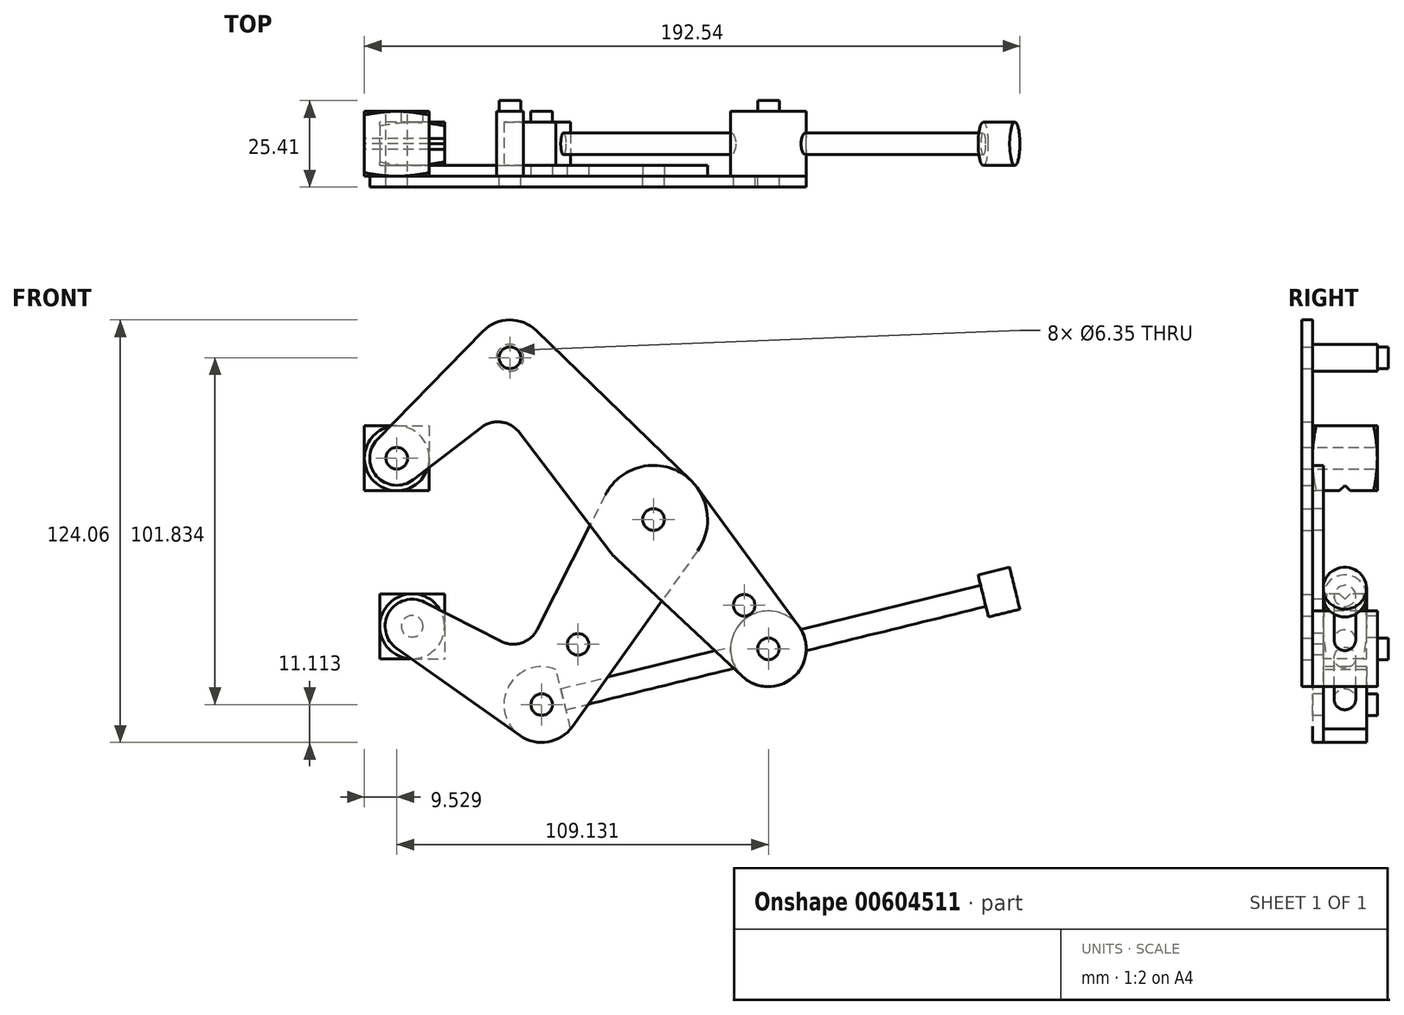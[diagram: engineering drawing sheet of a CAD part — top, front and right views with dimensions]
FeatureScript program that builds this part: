
annotation { "Feature Type Name" : "Feature", "Feature Type Description" : "" }
export const myFeature = defineFeature(function(context is Context, id is Id, definition is map)
    precondition{}
    {
        {
            var Q0;
            Q0=qCreatedBy(makeId("Front.planeOp"),FACE);
            var sketch = newSketch(context, id + "F0", { "sketchPlane" : qUnion([Q0])});
            skCircle(sketch, "E0", {"center": v(-64.57, 13.24) * mm, "radius": 7.94 * mm});
            skLineSegment(sketch, "E1", {"start": v(-64.57, 13.24) * mm, "end": v(-31.33, 42.76) * mm, "construction": true});
            skLineSegment(sketch, "E2", {"start": v(-31.33, 42.76) * mm, "end": v(10.83, -4.72) * mm, "construction": true});
            skLineSegment(sketch, "E3", {"start": v(10.83, -4.72) * mm, "end": v(44.56, -42.7) * mm, "construction": true});
            skCircle(sketch, "E4", {"center": v(10.83, -4.72) * mm, "radius": 15.88 * mm});
            skCircle(sketch, "E5", {"center": v(44.56, -42.7) * mm, "radius": 11.11 * mm});
            skCircle(sketch, "E6", {"center": v(-31.33, 42.76) * mm, "radius": 11.11 * mm});
            skCircle(sketch, "E7", {"center": v(10.83, -4.72) * mm, "radius": 3.98 * mm});
            skLineSegment(sketch, "E8", {"start": v(10.83, -4.72) * mm, "end": v(-22, -59.08) * mm, "construction": true});
            skLineSegment(sketch, "E9", {"start": v(-22, -59.08) * mm, "end": v(-60.05, -36.1) * mm, "construction": true});
            skCircle(sketch, "E10", {"center": v(-60.05, -36.1) * mm, "radius": 7.94 * mm});
            skCircle(sketch, "E11", {"center": v(-22, -59.08) * mm, "radius": 11.11 * mm});
            skLineSegment(sketch, "E12", {"start": v(-22, -59.08) * mm, "end": v(-11.33, -41.4) * mm, "construction": true});
            skCircle(sketch, "E13", {"center": v(-11.33, -41.4) * mm, "radius": 3.18 * mm});
            skLineSegment(sketch, "E14", {"start": v(10.83, -4.72) * mm, "end": v(35.08, -32.04) * mm, "construction": true});
            skLineSegment(sketch, "E15", {"start": v(35.08, -32.04) * mm, "end": v(37.46, -29.93) * mm, "construction": true});
            skCircle(sketch, "E16", {"center": v(37.46, -29.93) * mm, "radius": 3.17 * mm});
            skCircle(sketch, "E17", {"center": v(44.56, -42.7) * mm, "radius": 3.18 * mm});
            skCircle(sketch, "E18", {"center": v(-31.33, 42.76) * mm, "radius": 3.18 * mm});
            skCircle(sketch, "E19", {"center": v(10.83, -4.72) * mm, "radius": 3.18 * mm});
            skCircle(sketch, "E20", {"center": v(-64.57, 13.24) * mm, "radius": 3.18 * mm});
            skCircle(sketch, "E21", {"center": v(-60.05, -36.1) * mm, "radius": 3.18 * mm});
            skCircle(sketch, "E22", {"center": v(-22, -59.08) * mm, "radius": 3.18 * mm});
            skLineSegment(sketch, "E23", {"start": v(-70.25, 18.79) * mm, "end": v(-39.29, 50.52) * mm});
            skLineSegment(sketch, "E24", {"start": v(-59.74, 6.95) * mm, "end": v(-39.74, 22.3) * mm});
            skLineSegment(sketch, "E25", {"start": v(-23.6, 50.74) * mm, "end": v(21.88, 6.68) * mm});
            skLineSegment(sketch, "E26", {"start": v(-28.58, 20.8) * mm, "end": v(-1.8, -14.35) * mm});
            skPoint(sketch, "E27", {"position": v(-33.41, 27.15) * mm});
            skLineSegment(sketch, "E28", {"start": v(23.64, 4.66) * mm, "end": v(53.52, -36.14) * mm});
            skLineSegment(sketch, "E29", {"start": v(0, -16.33) * mm, "end": v(36.98, -50.83) * mm});
            skLineSegment(sketch, "E30", {"start": v(23.76, -13.93) * mm, "end": v(-12.95, -65.52) * mm});
            skLineSegment(sketch, "E31", {"start": v(-64.63, -42.58) * mm, "end": v(-28.42, -68.15) * mm});
            skLineSegment(sketch, "E32", {"start": v(-56.44, -29.02) * mm, "end": v(-34, -40.48) * mm});
            skLineSegment(sketch, "E33", {"start": v(-3.34, 2.44) * mm, "end": v(-23.28, -36.99) * mm});
            skPoint(sketch, "E34", {"position": v(-26.89, -44.1) * mm});
            skArc(sketch, "E35.filletArc", {"start": v(-28.58, 20.8) * mm, "mid": v(-33.85, 23.87) * mm, "end": v(-39.74, 22.3) * mm});
            skArc(sketch, "E36.filletArc", {"start": v(-34, -40.48) * mm, "mid": v(-27.91, -40.96) * mm, "end": v(-23.28, -36.99) * mm});
            skSolve(sketch);
        }
        {
            var Q0;
            Q0=makeQuery(id+"F0.imprint","IMPRINT",FACE,{"disambiguationData":[TD([[makeQuery(id+"F0.imprint","IMPRINT",EDGE,{"derivedFrom":sQuery(id+"F0.wireOp",EDGE,"E13")}),-1.0]])]});
            var Q1;
            {var subQ0=sQuery(id+"F0.wireOp",EDGE,"E26");var subQ1=sQuery(id+"F0.wireOp",EDGE,"E4");var subQ2=makeQuery(id+"F0.imprint","INTERSECT",VERTEX,{"derivedFrom":[subQ1,subQ0]});Q1=makeQuery(id+"F0.imprint","IMPRINT",FACE,{"disambiguationData":[TD([[makeQuery(id+"F0.imprint","IMPRINT",EDGE,{"disambiguationData":[TD([[subQ2,1.0]])],"derivedFrom":subQ1}),-1.0]])]});}
            var Q2;
            Q2=makeQuery(id+"F0.imprint","IMPRINT",FACE,{"disambiguationData":[TD([[makeQuery(id+"F0.imprint","IMPRINT",EDGE,{"derivedFrom":sQuery(id+"F0.wireOp",EDGE,"E7")}),-1.0]])]});
            var Q3;
            {var subQ0=sQuery(id+"F0.wireOp",EDGE,"E29");var subQ1=sQuery(id+"F0.wireOp",EDGE,"E4");var subQ2=makeQuery(id+"F0.imprint","INTERSECT",VERTEX,{"derivedFrom":[subQ1,subQ0]});Q3=makeQuery(id+"F0.imprint","IMPRINT",FACE,{"disambiguationData":[TD([[makeQuery(id+"F0.imprint","IMPRINT",EDGE,{"disambiguationData":[TD([[subQ2,-1.0]])],"derivedFrom":subQ1}),-1.0]])]});}
            var Q4;
            Q4=makeQuery(id+"F0.imprint","IMPRINT",FACE,{"disambiguationData":[TD([[makeQuery(id+"F0.imprint","IMPRINT",EDGE,{"derivedFrom":sQuery(id+"F0.wireOp",EDGE,"E21")}),-1.0]])]});
            var Q5;
            Q5=makeQuery(id+"F0.imprint","IMPRINT",FACE,{"disambiguationData":[TD([[makeQuery(id+"F0.imprint","IMPRINT",EDGE,{"derivedFrom":sQuery(id+"F0.wireOp",EDGE,"E22")}),-1.0]])]});
            var Q6;
            Q6=makeQuery(id+"F0.imprint","IMPRINT",FACE,{"disambiguationData":[TD([[makeQuery(id+"F0.imprint","IMPRINT",EDGE,{"derivedFrom":sQuery(id+"F0.wireOp",EDGE,"E7")}),1.0]])]});
            extrude(context, id + "F1", {"entities" : qUnion([Q0, Q1, Q2, Q3, Q4, Q5, Q6]), "oppositeDirection" : true, "depth" : 3.17 * mm, "offsetDistance" : 25.4 * mm});
        }
        {
            var Q0;
            {var subQ0=sQuery(id+"F0.wireOp",EDGE,"E23");Q0=makeQuery(id+"F0.imprint","IMPRINT",FACE,{"disambiguationData":[TD([[makeQuery(id+"F0.imprint","IMPRINT",EDGE,{"derivedFrom":subQ0}),-1.0]])]});}
            var Q1;
            Q1=makeQuery(id+"F0.imprint","IMPRINT",FACE,{"disambiguationData":[TD([[makeQuery(id+"F0.imprint","IMPRINT",EDGE,{"derivedFrom":sQuery(id+"F0.wireOp",EDGE,"E20")}),-1.0]])]});
            var Q2;
            Q2=makeQuery(id+"F0.imprint","IMPRINT",FACE,{"disambiguationData":[TD([[makeQuery(id+"F0.imprint","IMPRINT",EDGE,{"derivedFrom":sQuery(id+"F0.wireOp",EDGE,"E18")}),-1.0]])]});
            var Q3;
            Q3=makeQuery(id+"F0.imprint","IMPRINT",FACE,{"disambiguationData":[TD([[makeQuery(id+"F0.imprint","IMPRINT",EDGE,{"derivedFrom":sQuery(id+"F0.wireOp",EDGE,"E7")}),-1.0]])]});
            var Q4;
            {var subQ0=sQuery(id+"F0.wireOp",EDGE,"E26");var subQ1=sQuery(id+"F0.wireOp",EDGE,"E4");var subQ2=makeQuery(id+"F0.imprint","INTERSECT",VERTEX,{"derivedFrom":[subQ1,subQ0]});Q4=makeQuery(id+"F0.imprint","IMPRINT",FACE,{"disambiguationData":[TD([[makeQuery(id+"F0.imprint","IMPRINT",EDGE,{"disambiguationData":[TD([[subQ2,1.0]])],"derivedFrom":subQ1}),-1.0]])]});}
            var Q5;
            {var subQ0=sQuery(id+"F0.wireOp",EDGE,"E29");var subQ1=sQuery(id+"F0.wireOp",EDGE,"E4");var subQ2=makeQuery(id+"F0.imprint","INTERSECT",VERTEX,{"derivedFrom":[subQ1,subQ0]});Q5=makeQuery(id+"F0.imprint","IMPRINT",FACE,{"disambiguationData":[TD([[makeQuery(id+"F0.imprint","IMPRINT",EDGE,{"disambiguationData":[TD([[subQ2,-1.0]])],"derivedFrom":subQ1}),-1.0]])]});}
            var Q6;
            Q6=makeQuery(id+"F0.imprint","IMPRINT",FACE,{"disambiguationData":[TD([[makeQuery(id+"F0.imprint","IMPRINT",EDGE,{"derivedFrom":sQuery(id+"F0.wireOp",EDGE,"E7")}),1.0]])]});
            var Q7;
            Q7=makeQuery(id+"F0.imprint","IMPRINT",FACE,{"disambiguationData":[TD([[makeQuery(id+"F0.imprint","IMPRINT",EDGE,{"derivedFrom":sQuery(id+"F0.wireOp",EDGE,"E16")}),-1.0]])]});
            var Q8;
            Q8=makeQuery(id+"F0.imprint","IMPRINT",FACE,{"disambiguationData":[TD([[makeQuery(id+"F0.imprint","IMPRINT",EDGE,{"derivedFrom":sQuery(id+"F0.wireOp",EDGE,"E17")}),-1.0]])]});
            extrude(context, id + "F2", {"entities" : qUnion([Q0, Q1, Q2, Q3, Q4, Q5, Q6, Q7, Q8]), "depth" : 3.17 * mm, "offsetDistance" : 25.4 * mm});
        }
        {
            var Q0;
            Q0=makeQuery(id+"F2.opExtrude","CAP_FACE",FACE,{"disambiguationData":[OSD([sQuery(id+"F0.wireOp",EDGE,"E0"),sQuery(id+"F0.wireOp",EDGE,"E4"),sQuery(id+"F0.wireOp",EDGE,"E5"),sQuery(id+"F0.wireOp",EDGE,"E6"),sQuery(id+"F0.wireOp",EDGE,"E16"),sQuery(id+"F0.wireOp",EDGE,"E17"),sQuery(id+"F0.wireOp",EDGE,"E18"),sQuery(id+"F0.wireOp",EDGE,"E19"),sQuery(id+"F0.wireOp",EDGE,"E20"),sQuery(id+"F0.wireOp",EDGE,"E23"),sQuery(id+"F0.wireOp",EDGE,"E24"),sQuery(id+"F0.wireOp",EDGE,"E25"),sQuery(id+"F0.wireOp",EDGE,"E26"),sQuery(id+"F0.wireOp",EDGE,"E28"),sQuery(id+"F0.wireOp",EDGE,"E29"),sQuery(id+"F0.wireOp",EDGE,"E35.filletArc")])],"isStart":false});
            var sketch = newSketch(context, id + "F3", { "sketchPlane" : qUnion([Q0])});
            skCircle(sketch, "E37", {"center": v(-31.33, 42.76) * mm, "radius": 3.98 * mm});
            skCircle(sketch, "E38", {"center": v(10.83, -4.72) * mm, "radius": 3.98 * mm});
            skCircle(sketch, "E39", {"center": v(44.56, -42.7) * mm, "radius": 11.11 * mm});
            skSolve(sketch);
        }
        {
            var Q0;
            Q0=qCreatedBy(makeId("Front.planeOp"),FACE);
            var sketch = newSketch(context, id + "F4", { "sketchPlane" : qUnion([Q0])});
            skCircle(sketch, "E40", {"center": v(-60.05, -36.1) * mm, "radius": 3.98 * mm});
            skCircle(sketch, "E41", {"center": v(-22, -59.08) * mm, "radius": 11.11 * mm});
            skLineSegment(sketch, "E42", {"start": v(-15.65, -57.52) * mm, "end": v(44.56, -42.7) * mm, "construction": true});
            skLineSegment(sketch, "E43", {"start": v(-22, -59.08) * mm, "end": v(-15.65, -57.52) * mm, "construction": true});
            skLineSegment(sketch, "E44", {"start": v(-15.65, -57.52) * mm, "end": v(-17.8, -48.8) * mm});
            skLineSegment(sketch, "E45", {"start": v(-15.65, -57.52) * mm, "end": v(-13.5, -66.24) * mm});
            skPoint(sketch, "E46", {"position": v(44.56, -42.7) * mm});
            skSolve(sketch);
        }
        {
            var Q0;
            Q0=qCreatedBy(makeId("Front.planeOp"),FACE);
            cPlane(context, id + "F5", {"entities" : qUnion([Q0]), "cplaneType" : CPlaneType.OFFSET, "offset" : 9.52 * mm, "oppositeDirection" : true, "width" : 152.4 * mm, "height" : 152.4 * mm});
        }
        {
            var Q0;
            Q0=makeQuery(id+"F3.imprint","IMPRINT",FACE,{"disambiguationData":[TD([[makeQuery(id+"F3.imprint","IMPRINT",EDGE,{"derivedFrom":makeQuery(id+"F2.opExtrude","CAP_EDGE",EDGE,{"disambiguationData":[OSD([sQuery(id+"F0.wireOp",EDGE,"E17")])],"isStart":false})}),-1.0]])]});
            var Q1;
            Q1=makeQuery(id+"F3.imprint","IMPRINT",FACE,{"disambiguationData":[TD([[makeQuery(id+"F3.imprint","IMPRINT",EDGE,{"derivedFrom":sQuery(id+"F3.wireOp",EDGE,"E37")}),1.0]])]});
            var Q2;
            Q2=makeQuery(id+"F3.imprint","IMPRINT",FACE,{"disambiguationData":[TD([[makeQuery(id+"F3.imprint","IMPRINT",EDGE,{"derivedFrom":makeQuery(id+"F2.opExtrude","CAP_EDGE",EDGE,{"disambiguationData":[OSD([sQuery(id+"F0.wireOp",EDGE,"E18")])],"isStart":false})}),1.0]])]});
            var Q3;
            Q3=makeQuery(id+"F3.imprint","IMPRINT",FACE,{"disambiguationData":[TD([[makeQuery(id+"F3.imprint","IMPRINT",EDGE,{"derivedFrom":makeQuery(id+"F2.opExtrude","CAP_EDGE",EDGE,{"disambiguationData":[OSD([sQuery(id+"F0.wireOp",EDGE,"E17")])],"isStart":false})}),1.0]])]});
            var Q4;
            Q4=makeQuery(id+"F4.imprint","IMPRINT",FACE,{"disambiguationData":[TD([[makeQuery(id+"F4.imprint","IMPRINT",EDGE,{"derivedFrom":makeQuery(id+"F1.opExtrude","CAP_EDGE",EDGE,{"disambiguationData":[OSD([sQuery(id+"F0.wireOp",EDGE,"E21")])],"isStart":true})}),1.0]])]});
            var Q5;
            Q5=makeQuery(id+"F4.imprint","IMPRINT",FACE,{"disambiguationData":[TD([[makeQuery(id+"F4.imprint","IMPRINT",EDGE,{"derivedFrom":sQuery(id+"F4.wireOp",EDGE,"E40")}),1.0]])]});
            var Q6;
            {var subQ0=sQuery(id+"F4.wireOp",EDGE,"E44");Q6=makeQuery(id+"F4.imprint","IMPRINT",FACE,{"disambiguationData":[TD([[makeQuery(id+"F4.imprint","IMPRINT",EDGE,{"derivedFrom":subQ0}),1.0]])]});}
            var Q7;
            Q7=makeQuery(id+"F4.imprint","IMPRINT",FACE,{"disambiguationData":[TD([[makeQuery(id+"F4.imprint","IMPRINT",EDGE,{"derivedFrom":makeQuery(id+"F1.opExtrude","CAP_EDGE",EDGE,{"disambiguationData":[OSD([sQuery(id+"F0.wireOp",EDGE,"E22")])],"isStart":true})}),1.0]])]});
            var Q8;
            Q8=qCreatedBy(id+"F5.planeOp",FACE);
            extrude(context, id + "F6", {"entities" : qUnion([Q0, Q1, Q2, Q3, Q4, Q5, Q6, Q7]), "endBound" : BoundingType.UP_TO_SURFACE, "oppositeDirection" : true, "depth" : 25.4 * mm, "endBoundEntityFace" : qUnion([Q8]), "offsetDistance" : 25.4 * mm});
        }
        {
            var Q0;
            Q0=makeQuery(id+"F2.opExtrude","SWEPT_BODY",BODY,{"disambiguationData":[OSD([sQuery(id+"F0.wireOp",EDGE,"E0"),sQuery(id+"F0.wireOp",EDGE,"E4"),sQuery(id+"F0.wireOp",EDGE,"E5"),sQuery(id+"F0.wireOp",EDGE,"E6"),sQuery(id+"F0.wireOp",EDGE,"E16"),sQuery(id+"F0.wireOp",EDGE,"E17"),sQuery(id+"F0.wireOp",EDGE,"E18"),sQuery(id+"F0.wireOp",EDGE,"E19"),sQuery(id+"F0.wireOp",EDGE,"E20"),sQuery(id+"F0.wireOp",EDGE,"E23"),sQuery(id+"F0.wireOp",EDGE,"E24"),sQuery(id+"F0.wireOp",EDGE,"E25"),sQuery(id+"F0.wireOp",EDGE,"E26"),sQuery(id+"F0.wireOp",EDGE,"E28"),sQuery(id+"F0.wireOp",EDGE,"E29"),sQuery(id+"F0.wireOp",EDGE,"E35.filletArc")])]});
            var Q1;
            Q1=makeQuery(id+"F6.opExtrude","SWEPT_BODY",BODY,{"disambiguationData":[OSD([sQuery(id+"F3.wireOp",EDGE,"E39")])]});
            var Q2;
            Q2=makeQuery(id+"F6.opExtrude","SWEPT_BODY",BODY,{"disambiguationData":[OSD([sQuery(id+"F3.wireOp",EDGE,"E37")])]});
            booleanBodies(context, id + "F7", {"operationType" : BooleanOperationType.SUBTRACTION, "tools" : qUnion([Q0]), "targets" : qUnion([Q1, Q2]), "keepTools" : true});
        }
        {
            var Q0;
            Q0=makeQuery(id+"F1.opExtrude","SWEPT_BODY",BODY,{"disambiguationData":[OSD([sQuery(id+"F0.wireOp",EDGE,"E4"),sQuery(id+"F0.wireOp",EDGE,"E10"),sQuery(id+"F0.wireOp",EDGE,"E11"),sQuery(id+"F0.wireOp",EDGE,"E13"),sQuery(id+"F0.wireOp",EDGE,"E19"),sQuery(id+"F0.wireOp",EDGE,"E21"),sQuery(id+"F0.wireOp",EDGE,"E22"),sQuery(id+"F0.wireOp",EDGE,"E30"),sQuery(id+"F0.wireOp",EDGE,"E31"),sQuery(id+"F0.wireOp",EDGE,"E32"),sQuery(id+"F0.wireOp",EDGE,"E33"),sQuery(id+"F0.wireOp",EDGE,"E36.filletArc")])]});
            var Q1;
            Q1=makeQuery(id+"F6.opExtrude","SWEPT_BODY",BODY,{"disambiguationData":[OSD([sQuery(id+"F4.wireOp",EDGE,"E41"),sQuery(id+"F4.wireOp",EDGE,"E44"),sQuery(id+"F4.wireOp",EDGE,"E45")])]});
            var Q2;
            Q2=makeQuery(id+"F6.opExtrude","SWEPT_BODY",BODY,{"disambiguationData":[OSD([sQuery(id+"F4.wireOp",EDGE,"E40")])]});
            booleanBodies(context, id + "F8", {"operationType" : BooleanOperationType.SUBTRACTION, "tools" : qUnion([Q0]), "targets" : qUnion([Q1, Q2]), "keepTools" : true});
        }
        {
            var Q0;
            Q0=makeQuery(id+"F6.opExtrude","SWEPT_BODY",BODY,{"disambiguationData":[OSD([sQuery(id+"F3.wireOp",EDGE,"E37")])]});
            var Q1;
            Q1=makeQuery(id+"F6.opExtrude","SWEPT_BODY",BODY,{"disambiguationData":[OSD([sQuery(id+"F3.wireOp",EDGE,"E39")])]});
            var Q2;
            Q2=makeQuery(id+"F6.opExtrude","SWEPT_BODY",BODY,{"disambiguationData":[OSD([sQuery(id+"F4.wireOp",EDGE,"E41"),sQuery(id+"F4.wireOp",EDGE,"E44"),sQuery(id+"F4.wireOp",EDGE,"E45")])]});
            var Q3;
            Q3=makeQuery(id+"F6.opExtrude","SWEPT_BODY",BODY,{"disambiguationData":[OSD([sQuery(id+"F4.wireOp",EDGE,"E40")])]});
            var Q4;
            Q4=qCreatedBy(id+"F5.planeOp",FACE);
            mirror(context, id + "F9", {"entities" : qUnion([Q0, Q1, Q2, Q3]), "mirrorPlane" : qUnion([Q4])});
        }
        {
            var Q0;
            Q0=makeQuery(id+"F6.opExtrude","SWEPT_BODY",BODY,{"disambiguationData":[OSD([sQuery(id+"F3.wireOp",EDGE,"E37")])]});
            var Q1;
            Q1=makeQuery(id+"F9.opPattern","COPY",BODY,{"derivedFrom":makeQuery(id+"F6.opExtrude","SWEPT_BODY",BODY,{"disambiguationData":[OSD([sQuery(id+"F3.wireOp",EDGE,"E37")])]}),"instanceName":"1"});
            var Q2;
            Q2=makeQuery(id+"F6.opExtrude","SWEPT_BODY",BODY,{"disambiguationData":[OSD([sQuery(id+"F3.wireOp",EDGE,"E39")])]});
            var Q3;
            Q3=makeQuery(id+"F6.opExtrude","SWEPT_BODY",BODY,{"disambiguationData":[OSD([sQuery(id+"F4.wireOp",EDGE,"E40")])]});
            var Q4;
            Q4=makeQuery(id+"F6.opExtrude","SWEPT_BODY",BODY,{"disambiguationData":[OSD([sQuery(id+"F4.wireOp",EDGE,"E41"),sQuery(id+"F4.wireOp",EDGE,"E44"),sQuery(id+"F4.wireOp",EDGE,"E45")])]});
            var Q5;
            Q5=makeQuery(id+"F9.opPattern","COPY",BODY,{"derivedFrom":makeQuery(id+"F6.opExtrude","SWEPT_BODY",BODY,{"disambiguationData":[OSD([sQuery(id+"F3.wireOp",EDGE,"E39")])]}),"instanceName":"1"});
            var Q6;
            Q6=makeQuery(id+"F9.opPattern","COPY",BODY,{"derivedFrom":makeQuery(id+"F6.opExtrude","SWEPT_BODY",BODY,{"disambiguationData":[OSD([sQuery(id+"F4.wireOp",EDGE,"E40")])]}),"instanceName":"1"});
            var Q7;
            Q7=makeQuery(id+"F9.opPattern","COPY",BODY,{"derivedFrom":makeQuery(id+"F6.opExtrude","SWEPT_BODY",BODY,{"disambiguationData":[OSD([sQuery(id+"F4.wireOp",EDGE,"E41"),sQuery(id+"F4.wireOp",EDGE,"E44"),sQuery(id+"F4.wireOp",EDGE,"E45")])]}),"instanceName":"1"});
            booleanBodies(context, id + "F10", {"operationType" : BooleanOperationType.UNION, "tools" : qUnion([Q0, Q1, Q2, Q3, Q4, Q5, Q6, Q7])});
        }
        {
            var Q0;
            {var subQ0=makeQuery(id+"F6.opExtrude","SWEPT_FACE",FACE,{"disambiguationData":[OSD([sQuery(id+"F4.wireOp",EDGE,"E44"),sQuery(id+"F4.wireOp",EDGE,"E45")])]});Q0=makeQuery(id+"F10.opBoolean","MERGE",FACE,{"derivedFrom":[subQ0,makeQuery(id+"F9.opPattern","COPY",FACE,{"derivedFrom":subQ0,"instanceName":"1"})]});}
            var sketch = newSketch(context, id + "F11", { "sketchPlane" : qUnion([Q0])});
            skLineSegment(sketch, "E47", {"start": v(9.53, -61.1) * mm, "end": v(9.53, -43.13) * mm, "construction": true});
            skLineSegment(sketch, "E48", {"start": v(3.18, -52.11) * mm, "end": v(15.88, -52.11) * mm, "construction": true});
            skCircle(sketch, "E49", {"center": v(9.53, -52.11) * mm, "radius": 3.18 * mm});
            skSolve(sketch);
        }
        {
            var Q0;
            Q0=makeQuery(id+"F11.imprint","IMPRINT",FACE,{"disambiguationData":[TD([[makeQuery(id+"F11.imprint","IMPRINT",EDGE,{"derivedFrom":sQuery(id+"F11.wireOp",EDGE,"E49")}),1.0]])]});
            extrude(context, id + "F12", {"entities" : qUnion([Q0]), "oppositeDirection" : true, "depth" : 12.7 * mm, "offsetDistance" : 25.4 * mm});
        }
        {
            var Q0;
            Q0=makeQuery(id+"F12.opExtrude","CAP_FACE",FACE,{"disambiguationData":[OSD([sQuery(id+"F11.wireOp",EDGE,"E49")])],"isStart":true});
            extrude(context, id + "F13", {"entities" : qUnion([Q0]), "operationType" : NewBodyOperationType.ADD, "depth" : 127 * mm, "offsetDistance" : 25.4 * mm});
        }
        {
            var Q0;
            Q0=makeQuery(id+"F13.opExtrude","CAP_FACE",FACE,{"disambiguationData":[OSD([sQuery(id+"F11.wireOp",EDGE,"E49")])],"isStart":false});
            var sketch = newSketch(context, id + "F14", { "sketchPlane" : qUnion([Q0])});
            skCircle(sketch, "E50", {"center": v(9.53, -52.11) * mm, "radius": 6.35 * mm});
            skSolve(sketch);
        }
        {
            var Q0;
            Q0=makeQuery(id+"F14.imprint","IMPRINT",FACE,{"disambiguationData":[TD([[makeQuery(id+"F14.imprint","IMPRINT",EDGE,{"derivedFrom":sQuery(id+"F14.wireOp",EDGE,"E50")}),1.0]])]});
            var Q1;
            Q1=makeQuery(id+"F14.imprint","IMPRINT",FACE,{"disambiguationData":[TD([[makeQuery(id+"F14.imprint","IMPRINT",EDGE,{"derivedFrom":makeQuery(id+"F13.opExtrude","CAP_EDGE",EDGE,{"disambiguationData":[OSD([sQuery(id+"F11.wireOp",EDGE,"E49")])],"isStart":false})}),1.0]])]});
            extrude(context, id + "F15", {"entities" : qUnion([Q0, Q1]), "operationType" : NewBodyOperationType.ADD, "depth" : 9.52 * mm, "offsetDistance" : 25.4 * mm});
        }
        {
            var Q0;
            Q0=makeQuery(id+"F1.opExtrude","CAP_FACE",FACE,{"disambiguationData":[OSD([sQuery(id+"F0.wireOp",EDGE,"E4"),sQuery(id+"F0.wireOp",EDGE,"E10"),sQuery(id+"F0.wireOp",EDGE,"E11"),sQuery(id+"F0.wireOp",EDGE,"E13"),sQuery(id+"F0.wireOp",EDGE,"E19"),sQuery(id+"F0.wireOp",EDGE,"E21"),sQuery(id+"F0.wireOp",EDGE,"E22"),sQuery(id+"F0.wireOp",EDGE,"E30"),sQuery(id+"F0.wireOp",EDGE,"E31"),sQuery(id+"F0.wireOp",EDGE,"E32"),sQuery(id+"F0.wireOp",EDGE,"E33"),sQuery(id+"F0.wireOp",EDGE,"E36.filletArc")])],"isStart":false});
            var sketch = newSketch(context, id + "F16", { "sketchPlane" : qUnion([Q0])});
            skLineSegment(sketch, "E51.bottom", {"start": v(69.58, -26.57) * mm, "end": v(50.53, -26.57) * mm});
            skLineSegment(sketch, "E51.top", {"start": v(69.58, -45.62) * mm, "end": v(50.53, -45.62) * mm});
            skLineSegment(sketch, "E51.left", {"start": v(69.58, -26.57) * mm, "end": v(69.58, -45.62) * mm});
            skLineSegment(sketch, "E51.right", {"start": v(50.53, -26.57) * mm, "end": v(50.53, -45.62) * mm});
            skPoint(sketch, "E51.middle", {"position": v(60.05, -36.1) * mm});
            skPoint(sketch, "E52.middle", {"position": v(64.57, 13.24) * mm});
            skSolve(sketch);
        }
        {
            var Q0;
            {var subQ1=sQuery(id+"F16.wireOp",EDGE,"E51.bottom");Q0=makeQuery(id+"F16.imprint","IMPRINT",FACE,{"disambiguationData":[TD([[makeQuery(id+"F16.imprint","IMPRINT",EDGE,{"derivedFrom":subQ1}),1.0]])]});}
            var Q1;
            {var subQ5=makeQuery(id+"F1.opExtrude","CAP_EDGE",EDGE,{"disambiguationData":[OSD([sQuery(id+"F0.wireOp",EDGE,"E10")])],"isStart":false});Q1=makeQuery(id+"F16.imprint","IMPRINT",FACE,{"disambiguationData":[TD([[makeQuery(id+"F16.imprint","IMPRINT",EDGE,{"derivedFrom":subQ5}),-1.0]])]});}
            var Q2;
            Q2=qCreatedBy(id+"F5.planeOp",FACE);
            extrude(context, id + "F17", {"entities" : qUnion([Q0, Q1]), "endBound" : BoundingType.UP_TO_SURFACE, "depth" : 25.4 * mm, "endBoundEntityFace" : qUnion([Q2]), "offsetDistance" : 25.4 * mm});
        }
        {
            var Q0;
            Q0=makeQuery(id+"F2.opExtrude","CAP_FACE",FACE,{"disambiguationData":[OSD([sQuery(id+"F0.wireOp",EDGE,"E0"),sQuery(id+"F0.wireOp",EDGE,"E4"),sQuery(id+"F0.wireOp",EDGE,"E5"),sQuery(id+"F0.wireOp",EDGE,"E6"),sQuery(id+"F0.wireOp",EDGE,"E16"),sQuery(id+"F0.wireOp",EDGE,"E17"),sQuery(id+"F0.wireOp",EDGE,"E18"),sQuery(id+"F0.wireOp",EDGE,"E19"),sQuery(id+"F0.wireOp",EDGE,"E20"),sQuery(id+"F0.wireOp",EDGE,"E23"),sQuery(id+"F0.wireOp",EDGE,"E24"),sQuery(id+"F0.wireOp",EDGE,"E25"),sQuery(id+"F0.wireOp",EDGE,"E26"),sQuery(id+"F0.wireOp",EDGE,"E28"),sQuery(id+"F0.wireOp",EDGE,"E29"),sQuery(id+"F0.wireOp",EDGE,"E35.filletArc")])],"isStart":true});
            var sketch = newSketch(context, id + "F18", { "sketchPlane" : qUnion([Q0])});
            skLineSegment(sketch, "E53.bottom", {"start": v(74.1, 22.77) * mm, "end": v(55.05, 22.77) * mm});
            skLineSegment(sketch, "E53.top", {"start": v(74.1, 3.72) * mm, "end": v(55.05, 3.72) * mm});
            skLineSegment(sketch, "E53.left", {"start": v(74.1, 22.77) * mm, "end": v(74.1, 3.72) * mm});
            skLineSegment(sketch, "E53.right", {"start": v(55.05, 22.77) * mm, "end": v(55.05, 3.72) * mm});
            skPoint(sketch, "E53.middle", {"position": v(64.57, 13.24) * mm});
            skSolve(sketch);
        }
        {
            var Q0;
            {var subQ1=sQuery(id+"F18.wireOp",EDGE,"E53.top");Q0=makeQuery(id+"F18.imprint","IMPRINT",FACE,{"disambiguationData":[TD([[makeQuery(id+"F18.imprint","IMPRINT",EDGE,{"derivedFrom":subQ1}),-1.0]])]});}
            var Q1;
            {var subQ5=makeQuery(id+"F2.opExtrude","CAP_EDGE",EDGE,{"disambiguationData":[OSD([sQuery(id+"F0.wireOp",EDGE,"E0")])],"isStart":true});Q1=makeQuery(id+"F18.imprint","IMPRINT",FACE,{"disambiguationData":[TD([[makeQuery(id+"F18.imprint","IMPRINT",EDGE,{"derivedFrom":subQ5}),-1.0]])]});}
            var Q2;
            Q2=qCreatedBy(id+"F5.planeOp",FACE);
            extrude(context, id + "F19", {"entities" : qUnion([Q0, Q1]), "endBound" : BoundingType.UP_TO_SURFACE, "depth" : 25.4 * mm, "endBoundEntityFace" : qUnion([Q2]), "offsetDistance" : 25.4 * mm});
        }
        {
            var Q0;
            Q0=makeQuery(id+"F19.opExtrude","SWEPT_FACE",FACE,{"disambiguationData":[OSD([sQuery(id+"F18.wireOp",EDGE,"E53.bottom")])]});
            var sketch = newSketch(context, id + "F20", { "sketchPlane" : qUnion([Q0])});
            skLineSegment(sketch, "E54", {"start": v(-64.57, 9.53) * mm, "end": v(-64.57, 0) * mm});
            skSolve(sketch);
        }
        {
            var Q0;
            Q0=makeQuery(id+"F19.opExtrude","SWEPT_FACE",FACE,{"disambiguationData":[OSD([sQuery(id+"F18.wireOp",EDGE,"E53.left")])]});
            cPlane(context, id + "F21", {"entities" : qUnion([Q0]), "cplaneType" : CPlaneType.OFFSET, "offset" : 9.52 * mm, "oppositeDirection" : true, "width" : 152.4 * mm, "height" : 152.4 * mm});
        }
        {
            var Q0;
            Q0=qCreatedBy(id+"F21.planeOp",FACE);
            var sketch = newSketch(context, id + "F22", { "sketchPlane" : qUnion([Q0])});
            skLineSegment(sketch, "E55", {"start": v(0, 22.77) * mm, "end": v(0, 32.3) * mm});
            skLineSegment(sketch, "E56", {"start": v(0, 32.3) * mm, "end": v(-2.55, 32.3) * mm});
            skLineSegment(sketch, "E57", {"start": v(-2.55, 32.3) * mm, "end": v(0, 22.77) * mm});
            skSolve(sketch);
        }
        {
            var Q0;
            Q0=makeQuery(id+"F22.imprint","IMPRINT",FACE,{"disambiguationData":[TD([[makeQuery(id+"F22.imprint","IMPRINT",EDGE,{"derivedFrom":sQuery(id+"F22.wireOp",EDGE,"E55")}),1.0]])]});
            var Q1;
            Q1=makeQuery(id+"F19.opExtrude","CAP_EDGE",EDGE,{"disambiguationData":[OSD([sQuery(id+"F0.wireOp",EDGE,"E20")])],"isStart":false});
            revolve(context, id + "F23", {"operationType" : NewBodyOperationType.REMOVE, "entities" : qUnion([Q0]), "axis" : qUnion([Q1]), "revolveType" : RevolveType.FULL, "oppositeDirection" : true});
        }
        {
            var Q0;
            Q0=makeQuery(id+"F17.opExtrude","SWEPT_FACE",FACE,{"disambiguationData":[OSD([sQuery(id+"F16.wireOp",EDGE,"E51.bottom")])]});
            var sketch = newSketch(context, id + "F24", { "sketchPlane" : qUnion([Q0])});
            skLineSegment(sketch, "E58", {"start": v(-60.05, 9.53) * mm, "end": v(-60.05, 3.18) * mm});
            skSolve(sketch);
        }
        {
            var Q0;
            Q0=makeQuery(id+"F17.opExtrude","SWEPT_FACE",FACE,{"disambiguationData":[OSD([sQuery(id+"F16.wireOp",EDGE,"E51.left")])]});
            cPlane(context, id + "F25", {"entities" : qUnion([Q0]), "cplaneType" : CPlaneType.OFFSET, "offset" : 9.52 * mm, "oppositeDirection" : true, "width" : 152.4 * mm, "height" : 152.4 * mm});
        }
        {
            var Q0;
            Q0=qCreatedBy(id+"F25.planeOp",FACE);
            var sketch = newSketch(context, id + "F26", { "sketchPlane" : qUnion([Q0])});
            skLineSegment(sketch, "E59", {"start": v(-3.18, -26.57) * mm, "end": v(-3.18, -17.04) * mm});
            skLineSegment(sketch, "E60", {"start": v(-3.18, -17.04) * mm, "end": v(-5.73, -17.04) * mm});
            skLineSegment(sketch, "E61", {"start": v(-5.73, -17.04) * mm, "end": v(-3.18, -26.57) * mm});
            skSolve(sketch);
        }
        {
            var Q0;
            Q0=makeQuery(id+"F26.imprint","IMPRINT",FACE,{"disambiguationData":[TD([[makeQuery(id+"F26.imprint","IMPRINT",EDGE,{"derivedFrom":sQuery(id+"F26.wireOp",EDGE,"E59")}),1.0]])]});
            var Q1;
            Q1=makeQuery(id+"F1.opExtrude","CAP_EDGE",EDGE,{"disambiguationData":[OSD([sQuery(id+"F0.wireOp",EDGE,"E21")])],"isStart":true});
            revolve(context, id + "F27", {"operationType" : NewBodyOperationType.REMOVE, "entities" : qUnion([Q0]), "axis" : qUnion([Q1]), "revolveType" : RevolveType.FULL, "oppositeDirection" : true});
        }
        {
            var Q0;
            Q0=makeQuery(id+"F17.opExtrude","SWEPT_BODY",BODY,{"disambiguationData":[OSD([sQuery(id+"F0.wireOp",EDGE,"E21"),sQuery(id+"F16.wireOp",EDGE,"E51.bottom"),sQuery(id+"F16.wireOp",EDGE,"E51.top"),sQuery(id+"F16.wireOp",EDGE,"E51.left"),sQuery(id+"F16.wireOp",EDGE,"E51.right")])]});
            var Q1;
            Q1=makeQuery(id+"F17.opExtrude","CAP_FACE",FACE,{"disambiguationData":[OSD([sQuery(id+"F0.wireOp",EDGE,"E21"),sQuery(id+"F16.wireOp",EDGE,"E51.bottom"),sQuery(id+"F16.wireOp",EDGE,"E51.top"),sQuery(id+"F16.wireOp",EDGE,"E51.left"),sQuery(id+"F16.wireOp",EDGE,"E51.right")])],"isStart":false});
            mirror(context, id + "F28", {"operationType" : NewBodyOperationType.ADD, "entities" : qUnion([Q0]), "mirrorPlane" : qUnion([Q1])});
        }
        {
            var Q0;
            Q0=makeQuery(id+"F19.opExtrude","SWEPT_BODY",BODY,{"disambiguationData":[OSD([sQuery(id+"F0.wireOp",EDGE,"E20"),sQuery(id+"F18.wireOp",EDGE,"E53.bottom"),sQuery(id+"F18.wireOp",EDGE,"E53.top"),sQuery(id+"F18.wireOp",EDGE,"E53.left"),sQuery(id+"F18.wireOp",EDGE,"E53.right")])]});
            var Q1;
            Q1=makeQuery(id+"F19.opExtrude","CAP_FACE",FACE,{"disambiguationData":[OSD([sQuery(id+"F0.wireOp",EDGE,"E20"),sQuery(id+"F18.wireOp",EDGE,"E53.bottom"),sQuery(id+"F18.wireOp",EDGE,"E53.top"),sQuery(id+"F18.wireOp",EDGE,"E53.left"),sQuery(id+"F18.wireOp",EDGE,"E53.right")])],"isStart":false});
            mirror(context, id + "F29", {"operationType" : NewBodyOperationType.ADD, "entities" : qUnion([Q0]), "mirrorPlane" : qUnion([Q1])});
        }
        {
            var Q0;
            {var subQ0=makeQuery(id+"F17.opExtrude","SWEPT_FACE",FACE,{"disambiguationData":[OSD([sQuery(id+"F16.wireOp",EDGE,"E51.left")])]});Q0=makeQuery(id+"F28.boolean.opBoolean","MERGE",FACE,{"derivedFrom":[subQ0,makeQuery(id+"F28.opPattern","COPY",FACE,{"derivedFrom":subQ0,"instanceName":"1"})]});}
            var sketch = newSketch(context, id + "F30", { "sketchPlane" : qUnion([Q0])});
            skLineSegment(sketch, "E62", {"start": v(-9.52, -45.62) * mm, "end": v(-9.52, -28.17) * mm, "construction": true});
            skPoint(sketch, "E62.endSnap0", {"position": v(-9.53, -26.57) * mm});
            skLineSegment(sketch, "E63", {"start": v(-9.53, -28.17) * mm, "end": v(-9.53, -26.57) * mm});
            skLineSegment(sketch, "E64", {"start": v(-9.53, -28.17) * mm, "end": v(-11.13, -26.57) * mm});
            skLineSegment(sketch, "E65", {"start": v(-9.53, -28.17) * mm, "end": v(-7.92, -26.57) * mm});
            skSolve(sketch);
        }
        {
            var Q0;
            {var subQ0=sQuery(id+"F30.wireOp",EDGE,"E63");Q0=makeQuery(id+"F30.imprint","IMPRINT",FACE,{"disambiguationData":[TD([[makeQuery(id+"F30.imprint","IMPRINT",EDGE,{"derivedFrom":subQ0}),1.0]])]});}
            var Q1;
            {var subQ0=sQuery(id+"F30.wireOp",EDGE,"E63");Q1=makeQuery(id+"F30.imprint","IMPRINT",FACE,{"disambiguationData":[TD([[makeQuery(id+"F30.imprint","IMPRINT",EDGE,{"derivedFrom":subQ0}),-1.0]])]});}
            var Q2;
            Q2=sQuery(id+"F30.wireOp",EDGE,"E63");
            extrude(context, id + "F31", {"entities" : qUnion([Q0, Q1]), "operationType" : NewBodyOperationType.REMOVE, "surfaceEntities" : qUnion([Q2]), "oppositeDirection" : true, "depth" : 25.4 * mm, "offsetDistance" : 25.4 * mm});
        }
        {
            var Q0;
            {var subQ0=makeQuery(id+"F19.opExtrude","SWEPT_FACE",FACE,{"disambiguationData":[OSD([sQuery(id+"F18.wireOp",EDGE,"E53.left")])]});Q0=makeQuery(id+"F29.boolean.opBoolean","MERGE",FACE,{"derivedFrom":[subQ0,makeQuery(id+"F29.opPattern","COPY",FACE,{"derivedFrom":subQ0,"instanceName":"1"})]});}
            var sketch = newSketch(context, id + "F32", { "sketchPlane" : qUnion([Q0])});
            skLineSegment(sketch, "E66", {"start": v(-9.53, 22.77) * mm, "end": v(-9.52, 5.32) * mm, "construction": true});
            skLineSegment(sketch, "E67", {"start": v(-9.53, 5.32) * mm, "end": v(-9.53, 3.72) * mm});
            skLineSegment(sketch, "E68", {"start": v(-9.52, 5.32) * mm, "end": v(-11.13, 3.72) * mm});
            skLineSegment(sketch, "E69", {"start": v(-9.52, 5.32) * mm, "end": v(-7.92, 3.72) * mm});
            skSolve(sketch);
        }
        {
            var Q0;
            {var subQ0=sQuery(id+"F32.wireOp",EDGE,"E67");Q0=makeQuery(id+"F32.imprint","IMPRINT",FACE,{"disambiguationData":[TD([[makeQuery(id+"F32.imprint","IMPRINT",EDGE,{"derivedFrom":subQ0}),1.0]])]});}
            var Q1;
            {var subQ0=sQuery(id+"F32.wireOp",EDGE,"E67");Q1=makeQuery(id+"F32.imprint","IMPRINT",FACE,{"disambiguationData":[TD([[makeQuery(id+"F32.imprint","IMPRINT",EDGE,{"derivedFrom":subQ0}),-1.0]])]});}
            extrude(context, id + "F33", {"entities" : qUnion([Q0, Q1]), "operationType" : NewBodyOperationType.REMOVE, "oppositeDirection" : true, "depth" : 25.4 * mm, "offsetDistance" : 25.4 * mm});
        }
    });
